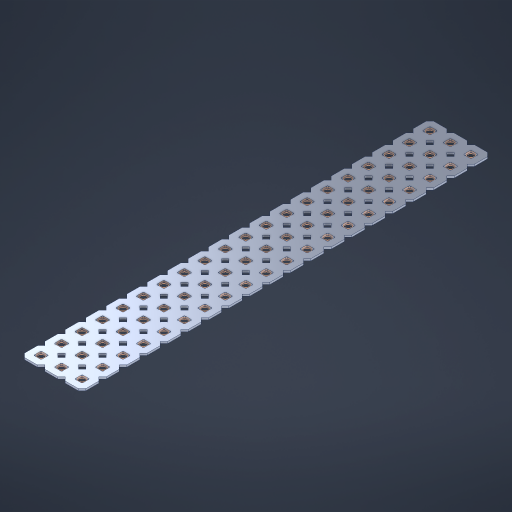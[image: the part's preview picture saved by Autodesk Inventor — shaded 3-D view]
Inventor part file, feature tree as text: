
AUTODESK INVENTOR PART (.ipt)
format: ipt  version: 2023 (Build 270158000, 158)  size: 953,344 bytes
history: native  units: in
note: dims shown in document units (in); Inventor stores cm internally (conversion verified against a paired STEP export)
features: other x61, extrude x59, sketch x2, pattern_linear x1
ambient origin geometry x8: Origin, YZ Plane, XZ Plane, XY Plane, X Axis, Y Axis, Z Axis, Center Point
bodies: Solid1 (feature_tree), Body (feature_tree)
feature tree (123):
  pattern_linear  "Rectangular Pattern1"  Spacing1=0.09in  [1 undecoded]
  sketch  "Sketch1"  dims[d1=0.5in]
  sketch  "Sketch2"  dims[d2=0.182in d3=0.09in d4=0.09in d5=0.09in d6=0.09in d7=0.09in d8=0.09in d9=0.09in d10=0.09in d11=0.02in d13=0.0in d14=0.172in d15=0.0625in d16=0.0in d19=0.5in d22=0.5in]
  other  "Srf1"
  other  "Srf126"
  other  "Srf127"
  other  "Srf128"
  other  "Srf129"
  other  "Srf130"
  other  "Srf131"
  other  "Srf250"
  other  "Srf251"
  other  "Srf252"
  other  "Srf253"
  other  "Srf254"
  other  "Srf255"
  other  "Srf256"
  other  "Srf257"
  other  "Srf258"
  other  "Srf259"
  other  "Srf260"
  other  "Srf261"
  other  "Srf262"
  other  "Srf268"
  other  "Srf269"
  other  "Srf270"
  other  "Srf271"
  other  "Srf272"
  other  "Srf273"
  other  "Srf274"
  other  "Srf275"
  other  "Srf276"
  other  "Srf277"
  other  "Srf278"
  other  "Srf279"
  other  "Srf280"
  other  "Srf281"
  other  "Srf282"
  other  "Srf283"
  other  "Srf284"
  other  "Srf285"
  other  "Srf286"
  other  "Srf287"
  other  "Srf293"
  other  "Srf294"
  other  "Srf295"
  other  "Srf296"
  other  "Srf297"
  other  "Srf298"
  other  "Srf299"
  other  "Srf300"
  other  "Srf301"
  other  "Srf302"
  other  "Srf303"
  other  "Srf304"
  other  "Srf305"
  other  "Srf306"
  other  "Srf307"
  other  "Srf308"
  other  "Srf309"
  other  "Srf310"
  other  "Srf311"
  other  "Srf312"
  other  "Circle"
  extrude  "ExtrusionSrf126"  Depth=0.09in
  extrude  "ExtrusionSrf127"  Depth=0.09in
  extrude  "ExtrusionSrf128"  Depth=0.09in
  extrude  "ExtrusionSrf129"  Depth=0.09in
  extrude  "ExtrusionSrf130"  Depth=0.09in
  extrude  "ExtrusionSrf131"  Depth=0.09in
  extrude  "ExtrusionSrf250"  Depth=0.09in
  extrude  "ExtrusionSrf251"  Depth=0.02in
  extrude  "ExtrusionSrf252"  TaperAngle=0.0deg  [1 undecoded]
  extrude  "ExtrusionSrf253"  Depth=0.5in
  extrude  "ExtrusionSrf254"  Depth=0.5in TaperAngle=0.0deg
  extrude  "ExtrusionSrf255"  Depth=0.5in
  extrude  "ExtrusionSrf256"  Depth=0.5in
  extrude  "ExtrusionSrf257"  [1 undecoded]
  extrude  "ExtrusionSrf258"  [1 undecoded]
  extrude  "ExtrusionSrf259"  [1 undecoded]
  extrude  "ExtrusionSrf260"  [1 undecoded]
  extrude  "ExtrusionSrf261"  [1 undecoded]
  extrude  "ExtrusionSrf262"  [1 undecoded]
  extrude  "ExtrusionSrf268"  [1 undecoded]
  extrude  "ExtrusionSrf269"  [1 undecoded]
  extrude  "ExtrusionSrf270"  [1 undecoded]
  extrude  "ExtrusionSrf271"  [1 undecoded]
  extrude  "ExtrusionSrf272"  [1 undecoded]
  extrude  "ExtrusionSrf273"  [1 undecoded]
  extrude  "ExtrusionSrf274"  [1 undecoded]
  extrude  "ExtrusionSrf275"  [1 undecoded]
  extrude  "ExtrusionSrf276"  [1 undecoded]
  extrude  "ExtrusionSrf277"  [1 undecoded]
  extrude  "ExtrusionSrf278"  [1 undecoded]
  extrude  "ExtrusionSrf279"  [1 undecoded]
  extrude  "ExtrusionSrf280"  [1 undecoded]
  extrude  "ExtrusionSrf281"  [1 undecoded]
  extrude  "ExtrusionSrf282"  [1 undecoded]
  extrude  "ExtrusionSrf283"  [1 undecoded]
  extrude  "ExtrusionSrf284"  [1 undecoded]
  extrude  "ExtrusionSrf285"  [1 undecoded]
  extrude  "ExtrusionSrf286"  [1 undecoded]
  extrude  "ExtrusionSrf287"  [1 undecoded]
  extrude  "ExtrusionSrf293"  [1 undecoded]
  extrude  "ExtrusionSrf294"  [1 undecoded]
  extrude  "ExtrusionSrf295"  [1 undecoded]
  extrude  "ExtrusionSrf296"  [1 undecoded]
  extrude  "ExtrusionSrf297"  [1 undecoded]
  extrude  "ExtrusionSrf298"  [1 undecoded]
  extrude  "ExtrusionSrf299"  [1 undecoded]
  extrude  "ExtrusionSrf300"  [1 undecoded]
  extrude  "ExtrusionSrf301"  [1 undecoded]
  extrude  "ExtrusionSrf302"  [1 undecoded]
  extrude  "ExtrusionSrf303"  [1 undecoded]
  extrude  "ExtrusionSrf304"  [1 undecoded]
  extrude  "ExtrusionSrf305"  [1 undecoded]
  extrude  "ExtrusionSrf306"  [1 undecoded]
  extrude  "ExtrusionSrf307"  [1 undecoded]
  extrude  "ExtrusionSrf308"  [1 undecoded]
  extrude  "ExtrusionSrf309"  [1 undecoded]
  extrude  "ExtrusionSrf310"  [1 undecoded]
  extrude  "ExtrusionSrf311"  [1 undecoded]
  extrude  "ExtrusionSrf312"  [1 undecoded]
note: 48 required parameter values undecoded (feature->parameter linkage not recoverable at this tier; creation-order binding heuristic only, values carry confidence <= 0.55)
